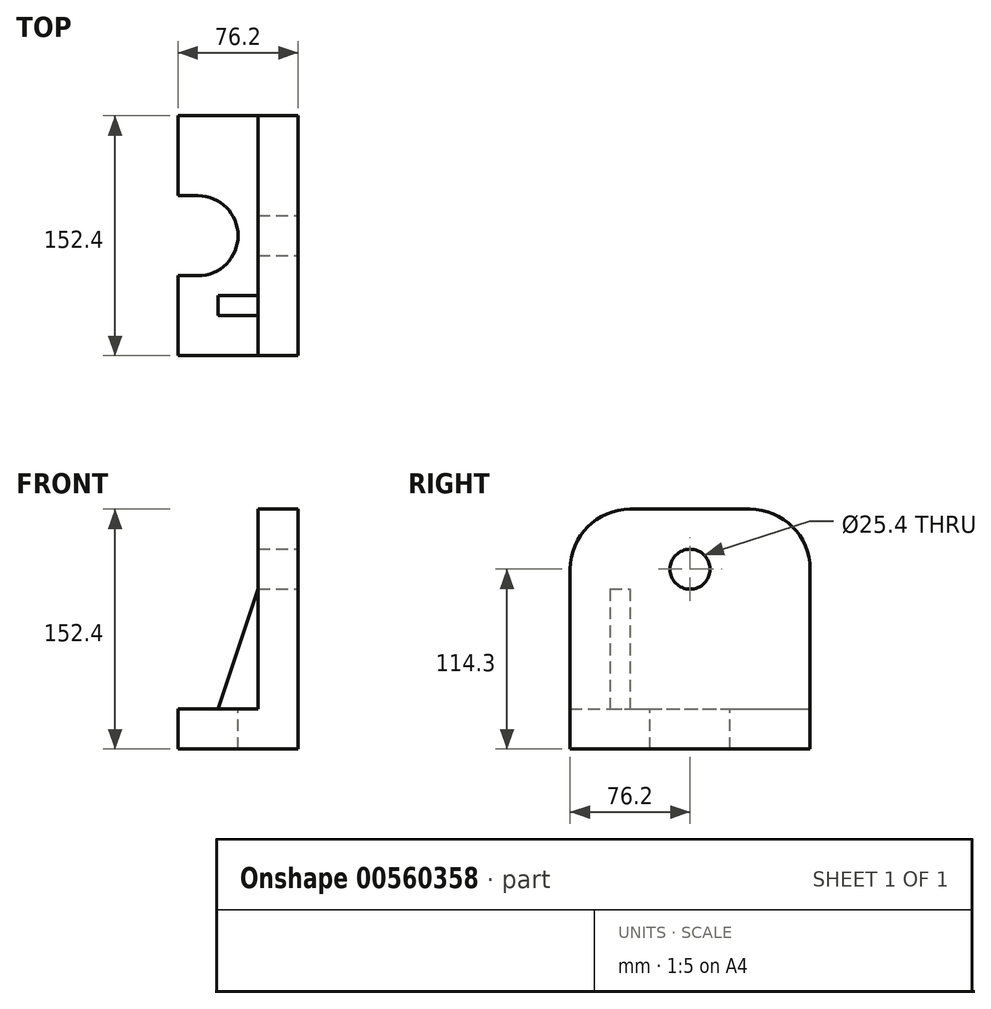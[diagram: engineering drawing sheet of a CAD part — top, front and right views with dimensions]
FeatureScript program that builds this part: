
annotation { "Feature Type Name" : "Feature", "Feature Type Description" : "" }
export const myFeature = defineFeature(function(context is Context, id is Id, definition is map)
    precondition{}
    {
        {
            var Q0;
            Q0=qCreatedBy(makeId("Front.planeOp"),FACE);
            var sketch = newSketch(context, id + "F0", { "sketchPlane" : qUnion([Q0])});
            skLineSegment(sketch, "E0", {"start": v(0, 0) * mm, "end": v(0, 152.4) * mm});
            skLineSegment(sketch, "E1", {"start": v(0, 152.4) * mm, "end": v(-25.4, 152.4) * mm});
            skLineSegment(sketch, "E2", {"start": v(-25.4, 152.4) * mm, "end": v(-25.4, 25.4) * mm});
            skLineSegment(sketch, "E3", {"start": v(-25.4, 25.4) * mm, "end": v(-76.2, 25.4) * mm});
            skLineSegment(sketch, "E4", {"start": v(-76.2, 25.4) * mm, "end": v(-76.2, 0) * mm});
            skLineSegment(sketch, "E5", {"start": v(-76.2, 0) * mm, "end": v(0, 0) * mm});
            skSolve(sketch);
        }
        {
            var Q0;
            Q0=makeQuery(id+"F0.imprint","IMPRINT",FACE,{"disambiguationData":[TD([[makeQuery(id+"F0.imprint","IMPRINT",EDGE,{"derivedFrom":sQuery(id+"F0.wireOp",EDGE,"E0")}),1.0]])]});
            extrude(context, id + "F1", {"entities" : qUnion([Q0]), "endBound" : BoundingType.SYMMETRIC, "depth" : 152.4 * mm, "offsetDistance" : 25.4 * mm});
        }
        {
            var Q0;
            Q0=qCreatedBy(makeId("Right.planeOp"),FACE);
            var sketch = newSketch(context, id + "F2", { "sketchPlane" : qUnion([Q0])});
            skCircle(sketch, "E6", {"center": v(0, 114.3) * mm, "radius": 12.7 * mm});
            skSolve(sketch);
        }
        {
            var Q0;
            Q0=makeQuery(id+"F2.imprint","IMPRINT",FACE,{"disambiguationData":[TD([[makeQuery(id+"F2.imprint","IMPRINT",EDGE,{"derivedFrom":sQuery(id+"F2.wireOp",EDGE,"E6")}),1.0]])]});
            extrude(context, id + "F3", {"entities" : qUnion([Q0]), "operationType" : NewBodyOperationType.REMOVE, "endBound" : BoundingType.THROUGH_ALL, "oppositeDirection" : true, "depth" : 25.4 * mm, "offsetDistance" : 25.4 * mm});
        }
        {
            var Q0;
            Q0=makeQuery(id+"F1.opExtrude","SWEPT_FACE",FACE,{"disambiguationData":[OSD([sQuery(id+"F0.wireOp",EDGE,"E3")])]});
            var sketch = newSketch(context, id + "F4", { "sketchPlane" : qUnion([Q0])});
            skLineSegment(sketch, "E7", {"start": v(-76.2, 25.4) * mm, "end": v(-63.5, 25.4) * mm});
            skLineSegment(sketch, "E8", {"start": v(-76.2, -25.4) * mm, "end": v(-63.5, -25.4) * mm});
            skArc(sketch, "E9", {"start": v(-63.5, -25.4) * mm, "mid": v(-38.1, 0) * mm, "end": v(-63.5, 25.4) * mm});
            skSolve(sketch);
        }
        {
            var Q0;
            {var subQ0=sQuery(id+"F4.wireOp",EDGE,"E7");Q0=makeQuery(id+"F4.imprint","IMPRINT",FACE,{"disambiguationData":[TD([[makeQuery(id+"F4.imprint","IMPRINT",EDGE,{"derivedFrom":subQ0}),-1.0]])]});}
            extrude(context, id + "F5", {"entities" : qUnion([Q0]), "operationType" : NewBodyOperationType.REMOVE, "endBound" : BoundingType.THROUGH_ALL, "oppositeDirection" : true, "depth" : 25.4 * mm, "offsetDistance" : 25.4 * mm});
        }
        {
            var Q0;
            Q0=makeQuery(id+"F1.opExtrude","CAP_EDGE",EDGE,{"disambiguationData":[OSD([sQuery(id+"F0.wireOp",EDGE,"E1")])],"isStart":false});
            var Q1;
            Q1=makeQuery(id+"F1.opExtrude","CAP_EDGE",EDGE,{"disambiguationData":[OSD([sQuery(id+"F0.wireOp",EDGE,"E1")])],"isStart":true});
            fillet(context, id + "F6", {"entities" : qUnion([Q0, Q1]), "radius" : 38.1 * mm, "tangentPropagation" : true, "allowEdgeOverflow" : false});
        }
        {
            var Q0;
            Q0=qCreatedBy(makeId("Front.planeOp"),FACE);
            cPlane(context, id + "F7", {"entities" : qUnion([Q0]), "cplaneType" : CPlaneType.OFFSET, "offset" : 44.45 * mm, "width" : 152.4 * mm, "height" : 152.4 * mm});
        }
        {
            var Q0;
            Q0=qCreatedBy(id+"F7.planeOp",FACE);
            var sketch = newSketch(context, id + "F8", { "sketchPlane" : qUnion([Q0])});
            skLineSegment(sketch, "E10.0", {"start": v(-25.4, 25.4) * mm, "end": v(-76.2, 25.4) * mm});
            skLineSegment(sketch, "E11.0", {"start": v(-25.4, 114.3) * mm, "end": v(-25.4, 25.4) * mm});
            skLineSegment(sketch, "E12", {"start": v(-25.4, 101.6) * mm, "end": v(-50.8, 25.4) * mm});
            skSolve(sketch);
        }
        {
            var Q0;
            {var subQ3=sQuery(id+"F8.wireOp",EDGE,"E12");Q0=makeQuery(id+"F8.imprint","IMPRINT",FACE,{"disambiguationData":[TD([[makeQuery(id+"F8.imprint","IMPRINT",EDGE,{"derivedFrom":subQ3}),1.0]])]});}
            extrude(context, id + "F9", {"entities" : qUnion([Q0]), "operationType" : NewBodyOperationType.ADD, "endBound" : BoundingType.SYMMETRIC, "depth" : 12.7 * mm, "offsetDistance" : 25.4 * mm});
        }
    });
